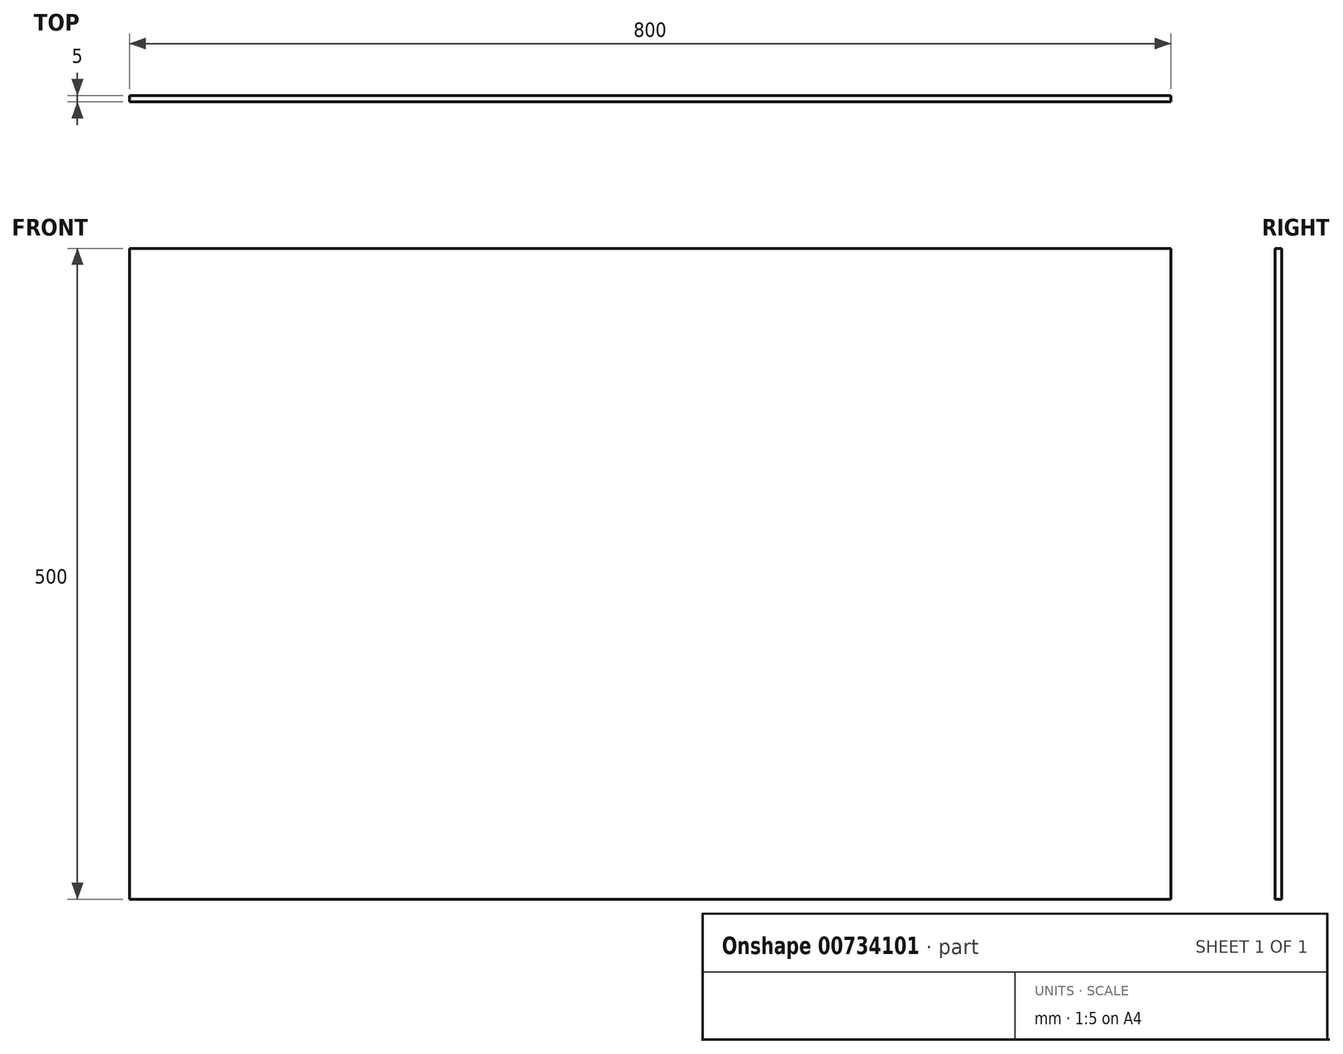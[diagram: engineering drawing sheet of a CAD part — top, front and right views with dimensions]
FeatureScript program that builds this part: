
annotation { "Feature Type Name" : "Feature", "Feature Type Description" : "" }
export const myFeature = defineFeature(function(context is Context, id is Id, definition is map)
    precondition{}
    {
        {
            var Q0;
            Q0=qCreatedBy(makeId("Front.planeOp"),FACE);
            var sketch = newSketch(context, id + "F0", { "sketchPlane" : qUnion([Q0])});
            skLineSegment(sketch, "E0.bottom", {"start": v(-105.56, 442.73) * mm, "end": v(694.44, 442.73) * mm});
            skLineSegment(sketch, "E0.top", {"start": v(-105.56, -57.27) * mm, "end": v(694.44, -57.27) * mm});
            skLineSegment(sketch, "E0.left", {"start": v(-105.56, 442.73) * mm, "end": v(-105.56, -57.27) * mm});
            skLineSegment(sketch, "E0.right", {"start": v(694.44, 442.73) * mm, "end": v(694.44, -57.27) * mm});
            skSolve(sketch);
        }
        {
            var Q0;
            Q0=makeQuery(id+"F0.imprint","IMPRINT",FACE,{"disambiguationData":[TD([[makeQuery(id+"F0.imprint","IMPRINT",EDGE,{"derivedFrom":sQuery(id+"F0.wireOp",EDGE,"E0.bottom")}),-1.0]])]});
            extrude(context, id + "F1", {"entities" : qUnion([Q0]), "depth" : 5 * mm, "offsetDistance" : 25 * mm});
        }
    });
